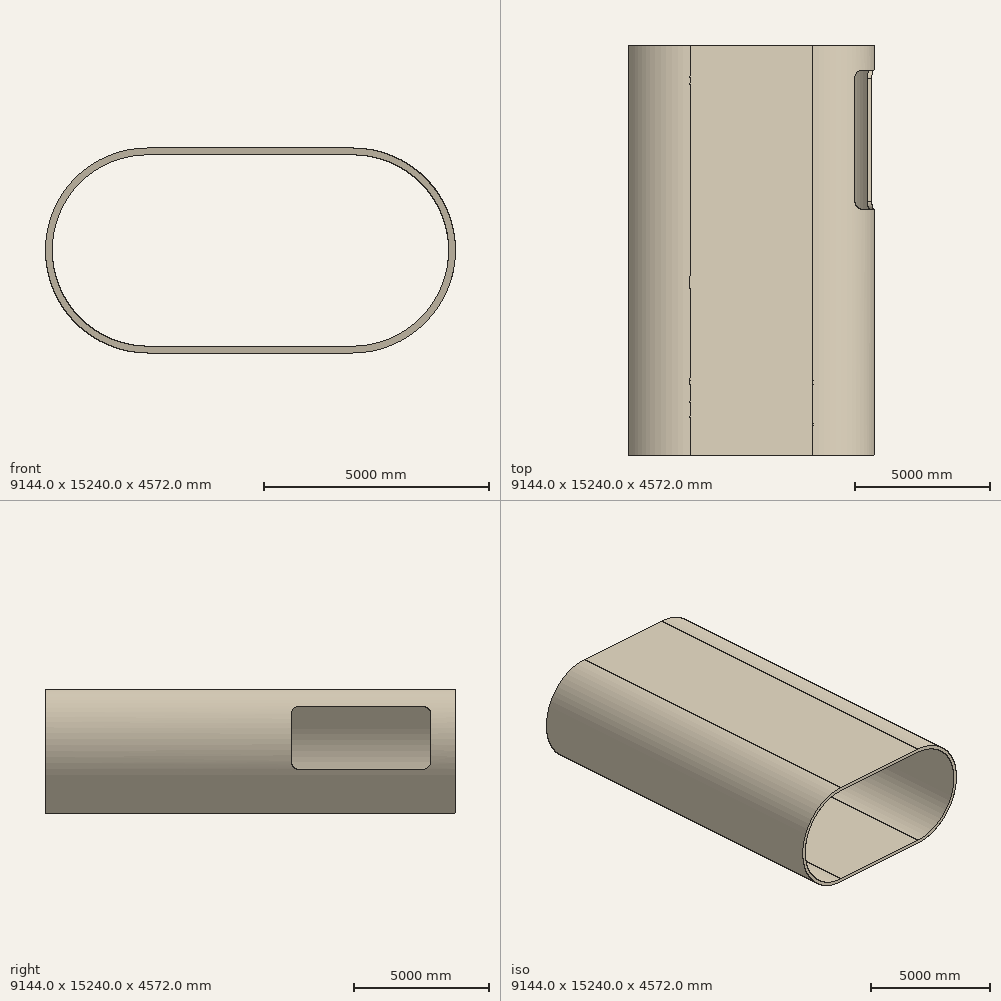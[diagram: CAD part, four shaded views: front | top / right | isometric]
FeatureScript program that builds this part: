
annotation { "Feature Type Name" : "Feature", "Feature Type Description" : "" }
export const myFeature = defineFeature(function(context is Context, id is Id, definition is map)
    precondition{}
    {
        {
            var Q0;
            Q0=qCreatedBy(makeId("Front.planeOp"),FACE);
            var sketch = newSketch(context, id + "F0", { "sketchPlane" : qUnion([Q0])});
            skArc(sketch, "E0", {"start": v(2738.77, -2063.03) * mm, "mid": v(5024.77, 222.97) * mm, "end": v(2738.77, 2508.97) * mm});
            skArc(sketch, "E1", {"start": v(-1833.23, 2508.97) * mm, "mid": v(-4119.23, 222.97) * mm, "end": v(-1833.23, -2063.03) * mm});
            skLineSegment(sketch, "E2.bottom", {"start": v(-1833.23, 2508.97) * mm, "end": v(2738.77, 2508.97) * mm});
            skLineSegment(sketch, "E2.top", {"start": v(-1833.23, -2063.03) * mm, "end": v(2738.77, -2063.03) * mm});
            skArc(sketch, "E3", {"start": v(2738.77, -1910.63) * mm, "mid": v(4872.37, 222.97) * mm, "end": v(2738.77, 2356.57) * mm});
            skArc(sketch, "E4", {"start": v(-1833.23, 2356.57) * mm, "mid": v(-3966.83, 222.97) * mm, "end": v(-1833.23, -1910.63) * mm});
            skLineSegment(sketch, "E5.bottom", {"start": v(-1833.23, 2356.57) * mm, "end": v(2738.77, 2356.57) * mm});
            skLineSegment(sketch, "E5.top", {"start": v(-1833.23, -1910.63) * mm, "end": v(2738.77, -1910.63) * mm});
            skSolve(sketch);
        }
        {
            var Q0;
            Q0=makeQuery(id+"F0.imprint","IMPRINT",FACE,{"disambiguationData":[TD([[makeQuery(id+"F0.imprint","IMPRINT",EDGE,{"derivedFrom":sQuery(id+"F0.wireOp",EDGE,"E0")}),1.0]])]});
            extrude(context, id + "F1", {"entities" : qUnion([Q0]), "depth" : 15240 * mm, "offsetDistance" : 30.48 * mm});
        }
        {
            var Q0;
            Q0=qCreatedBy(makeId("Right.planeOp"),FACE);
            var sketch = newSketch(context, id + "F2", { "sketchPlane" : qUnion([Q0])});
            skLineSegment(sketch, "E6.bottom", {"start": v(-5791.2, 1899.37) * mm, "end": v(-1219.2, 1899.37) * mm});
            skLineSegment(sketch, "E6.top", {"start": v(-5791.2, -447.59) * mm, "end": v(-1219.2, -447.59) * mm});
            skLineSegment(sketch, "E6.left", {"start": v(-6096, 1594.57) * mm, "end": v(-6096, -142.79) * mm});
            skLineSegment(sketch, "E6.right", {"start": v(-914.4, 1594.57) * mm, "end": v(-914.4, -142.79) * mm});
            skPoint(sketch, "E7.visualSharp", {"position": v(-914.4, 1899.37) * mm});
            skArc(sketch, "E7.filletArc", {"start": v(-914.4, 1594.57) * mm, "mid": v(-1003.67, 1810.1) * mm, "end": v(-1219.2, 1899.37) * mm});
            skPoint(sketch, "E8.visualSharp", {"position": v(-914.4, -447.59) * mm});
            skArc(sketch, "E8.filletArc", {"start": v(-1219.2, -447.59) * mm, "mid": v(-1003.67, -358.32) * mm, "end": v(-914.4, -142.79) * mm});
            skPoint(sketch, "E9.visualSharp", {"position": v(-6096, -447.59) * mm});
            skArc(sketch, "E9.filletArc", {"start": v(-6096, -142.79) * mm, "mid": v(-6006.73, -358.32) * mm, "end": v(-5791.2, -447.59) * mm});
            skPoint(sketch, "E10.visualSharp", {"position": v(-6096, 1899.37) * mm});
            skArc(sketch, "E10.filletArc", {"start": v(-5791.2, 1899.37) * mm, "mid": v(-6006.73, 1810.1) * mm, "end": v(-6096, 1594.57) * mm});
            skSolve(sketch);
        }
        {
            var Q0;
            Q0=makeQuery(id+"F2.imprint","IMPRINT",FACE,{"disambiguationData":[TD([[makeQuery(id+"F2.imprint","IMPRINT",EDGE,{"derivedFrom":sQuery(id+"F2.wireOp",EDGE,"E6.bottom")}),-1.0]])]});
            extrude(context, id + "F3", {"entities" : qUnion([Q0]), "operationType" : NewBodyOperationType.REMOVE, "depth" : 6096 * mm, "offsetDistance" : 30.48 * mm});
        }
    });
